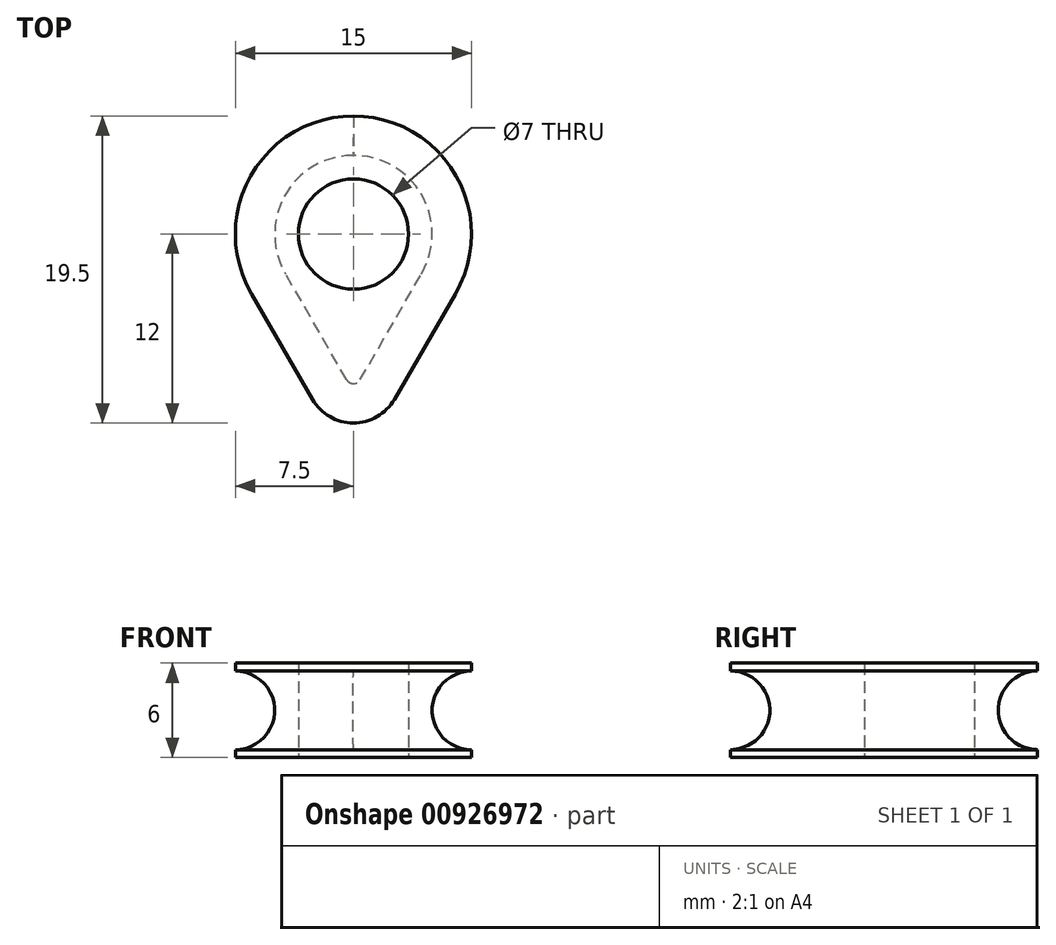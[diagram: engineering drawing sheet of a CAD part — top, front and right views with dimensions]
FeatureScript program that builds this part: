
annotation { "Feature Type Name" : "Feature", "Feature Type Description" : "" }
export const myFeature = defineFeature(function(context is Context, id is Id, definition is map)
    precondition{}
    {
        {
            var Q0;
            Q0=qCreatedBy(makeId("Top.planeOp"),FACE);
            var sketch = newSketch(context, id + "F0", { "sketchPlane" : qUnion([Q0])});
            skLineSegment(sketch, "E0", {"start": v(0, 71.12) * mm, "end": v(0, -85.72) * mm});
            skLineSegment(sketch, "E1", {"start": v(-6.47, -3.8) * mm, "end": v(-2.6, -10.5) * mm});
            skPoint(sketch, "E2.newPointA", {"position": v(2.17, -18.75) * mm});
            skPoint(sketch, "E2.newPointB", {"position": v(-2.17, -18.75) * mm});
            skArc(sketch, "E2.filletArc", {"start": v(-2.6, -10.5) * mm, "mid": v(-1.5, -11.6) * mm, "end": v(0, -12) * mm});
            skArc(sketch, "E3", {"start": v(0, 3.5) * mm, "mid": v(-3.5, 0) * mm, "end": v(0, -3.5) * mm});
            skArc(sketch, "E4.trimOffspring", {"start": v(0, 7.5) * mm, "mid": v(-6.5, 3.73) * mm, "end": v(-6.47, -3.8) * mm});
            skPoint(sketch, "E5.MirrorCS.start.orphan", {"position": v(6.47, -3.8) * mm});
            skSolve(sketch);
        }
        {
            var Q0;
            Q0=makeQuery(id+"F0.imprint","IMPRINT",FACE,{"disambiguationData":[TD([[makeQuery(id+"F0.imprint","IMPRINT",EDGE,{"derivedFrom":sQuery(id+"F0.wireOp",EDGE,"E1")}),1.0]])]});
            extrude(context, id + "F1", {"entities" : qUnion([Q0]), "depth" : 6 * mm, "offsetDistance" : 25 * mm});
        }
        {
            var Q0;
            Q0=makeQuery(id+"F1.opExtrude","SWEPT_EDGE",EDGE,{"disambiguationData":[OSD([sQuery(id+"F0.wireOp",EDGE,"E1"),sQuery(id+"F0.wireOp",EDGE,"E2.filletArc")])]});
            cPlane(context, id + "F2", {"entities" : qUnion([Q0]), "cplaneType" : CPlaneType.LINE_ANGLE, "offset" : 25 * mm, "angle" : 120 * degree, "oppositeDirection" : true, "width" : 150 * mm, "height" : 150 * mm});
        }
        {
            var Q0;
            Q0=qCreatedBy(id+"F2.planeOp",FACE);
            var sketch = newSketch(context, id + "F3", { "sketchPlane" : qUnion([Q0])});
            skLineSegment(sketch, "E6.0", {"start": v(-7.5, 5.5) * mm, "end": v(-7.5, 0.5) * mm});
            skArc(sketch, "E7", {"start": v(-7.5, 0.5) * mm, "mid": v(-5, 3) * mm, "end": v(-7.5, 5.5) * mm});
            skSolve(sketch);
        }
        {
            var Q0;
            Q0 = qSketchRegion(id + "F3", true);
            var Q1;
            Q1=makeQuery(id+"F1.opExtrude","CAP_EDGE",EDGE,{"disambiguationData":[OSD([sQuery(id+"F0.wireOp",EDGE,"E1")])],"isStart":true});
            sweep(context, id + "F4", {"operationType" : NewBodyOperationType.REMOVE, "profiles" : qUnion([Q0]), "path" : qUnion([Q1])});
        }
        {
            var Q0;
            {var subQ0=sQuery(id+"F0.wireOp",EDGE,"E1");var subQ1=sQuery(id+"F0.wireOp",EDGE,"rfZURpDM-tLdR-XXqh-Cgjc-WUFFaBA5o6mJ");Q0=makeQuery(id+"F4.boolean.opBoolean","MERGE",EDGE,{"derivedFrom":[makeQuery(id+"F1.opExtrude","SWEPT_EDGE",EDGE,{"disambiguationData":[OSD([subQ1,subQ0])]})],"fromTools":[makeQuery(id+"F4.opSweep","CAP_EDGE",EDGE,{"disambiguationData":[OSD([subQ1,subQ0,sQuery(id+"F3.wireOp",EDGE,"E6.0")])],"isStart":false})]});}
            cPlane(context, id + "F5", {"entities" : qUnion([Q0]), "cplaneType" : CPlaneType.LINE_ANGLE, "offset" : 30 * mm, "angle" : 60 * degree, "width" : 150 * mm, "height" : 150 * mm});
        }
        {
            var Q0;
            Q0=qCreatedBy(id+"F5.planeOp",FACE);
            var sketch = newSketch(context, id + "F6", { "sketchPlane" : qUnion([Q0])});
            skLineSegment(sketch, "E8.0.0", {"start": v(7.5, 0.5) * mm, "end": v(7.5, 5.5) * mm});
            skArc(sketch, "E8.0.1", {"start": v(7.5, 5.5) * mm, "mid": v(5, 3) * mm, "end": v(7.5, 0.5) * mm});
            skSolve(sketch);
        }
        {
            var Q0;
            Q0=makeQuery(id+"F6.imprint","IMPRINT",FACE,{"disambiguationData":[TD([[makeQuery(id+"F6.imprint","IMPRINT",EDGE,{"derivedFrom":sQuery(id+"F6.wireOp",EDGE,"E8.0.0")}),1.0]])]});
            var Q1;
            Q1=sQuery(id+"F0.wireOp",EDGE,"E4.trimOffspring");
            sweep(context, id + "F7", {"operationType" : NewBodyOperationType.REMOVE, "profiles" : qUnion([Q0]), "path" : qUnion([Q1])});
        }
        {
            var Q0;
            {var subQ0=sQuery(id+"F0.wireOp",EDGE,"E0");Q0=makeQuery(id+"F1.opExtrude","SWEPT_FACE",FACE,{"disambiguationData":[OSD([subQ0]),TDD([makeQuery(id+"F0.imprint","IMPRINT",EDGE,{"disambiguationData":[TD([[makeQuery(id+"F0.imprint","INTERSECT",VERTEX,{"disambiguationData":[OD(0.0)],"derivedFrom":[subQ0,sQuery(id+"F0.wireOp",EDGE,"E3")]}),1.0]])],"derivedFrom":subQ0})])]});}
            var sketch = newSketch(context, id + "F8", { "sketchPlane" : qUnion([Q0])});
            skEllipticalArc(sketch, "E9.0", {});
            skLineSegment(sketch, "E10.0", {"start": v(7.5, 0.5) * mm, "end": v(7.5, 5.5) * mm});
            const initialGuessF8  = {"E9.0": [0.0075, 0.003, 0, 1, 0.0025, 0.0024999399616993925, 0, 3.141592653589793]};
            skSetInitialGuess(sketch, initialGuessF8);
            skSolve(sketch);
        }
        {
            var Q0;
            Q0 = qSketchRegion(id + "F8", true);
            extrude(context, id + "F9", {"entities" : qUnion([Q0]), "operationType" : NewBodyOperationType.REMOVE, "oppositeDirection" : true, "depth" : 25 * mm, "offsetDistance" : 25 * mm});
        }
        {
            var Q0;
            Q0=makeQuery(id+"F4.boolean.opBoolean","COPY",FACE,{"derivedFrom":makeQuery(id+"F4.opSweep","CAP_FACE",FACE,{"disambiguationData":[OSD([sQuery(id+"F0.wireOp",EDGE,"E1"),sQuery(id+"F0.wireOp",EDGE,"E2.filletArc"),sQuery(id+"F3.wireOp",EDGE,"E6.0"),sQuery(id+"F3.wireOp",EDGE,"E7")])],"isStart":true})});
            var sketch = newSketch(context, id + "F10", { "sketchPlane" : qUnion([Q0])});
            skLineSegment(sketch, "E11.0.0", {"start": v(7.5, 0.5) * mm, "end": v(7.5, 5.5) * mm});
            skArc(sketch, "E11.0.1", {"start": v(7.5, 5.5) * mm, "mid": v(5, 3) * mm, "end": v(7.5, 0.5) * mm});
            skSolve(sketch);
        }
        {
            var Q0;
            Q0 = qSketchRegion(id + "F10", true);
            var Q1;
            Q1=sQuery(id+"F0.wireOp",EDGE,"E2.filletArc");
            sweep(context, id + "F11", {"operationType" : NewBodyOperationType.REMOVE, "profiles" : qUnion([Q0]), "path" : qUnion([Q1])});
        }
        {
            var Q0;
            Q0=makeQuery(id+"F1.opExtrude","SWEPT_BODY",BODY,{"disambiguationData":[OSD([sQuery(id+"F0.wireOp",EDGE,"E0"),sQuery(id+"F0.wireOp",EDGE,"E1"),sQuery(id+"F0.wireOp",EDGE,"E2.filletArc"),sQuery(id+"F0.wireOp",EDGE,"E3"),sQuery(id+"F0.wireOp",EDGE,"E4.trimOffspring")])]});
            var Q1;
            Q1=qCreatedBy(makeId("Right.planeOp"),FACE);
            mirror(context, id + "F12", {"operationType" : NewBodyOperationType.ADD, "entities" : qUnion([Q0]), "mirrorPlane" : qUnion([Q1])});
        }
    });
